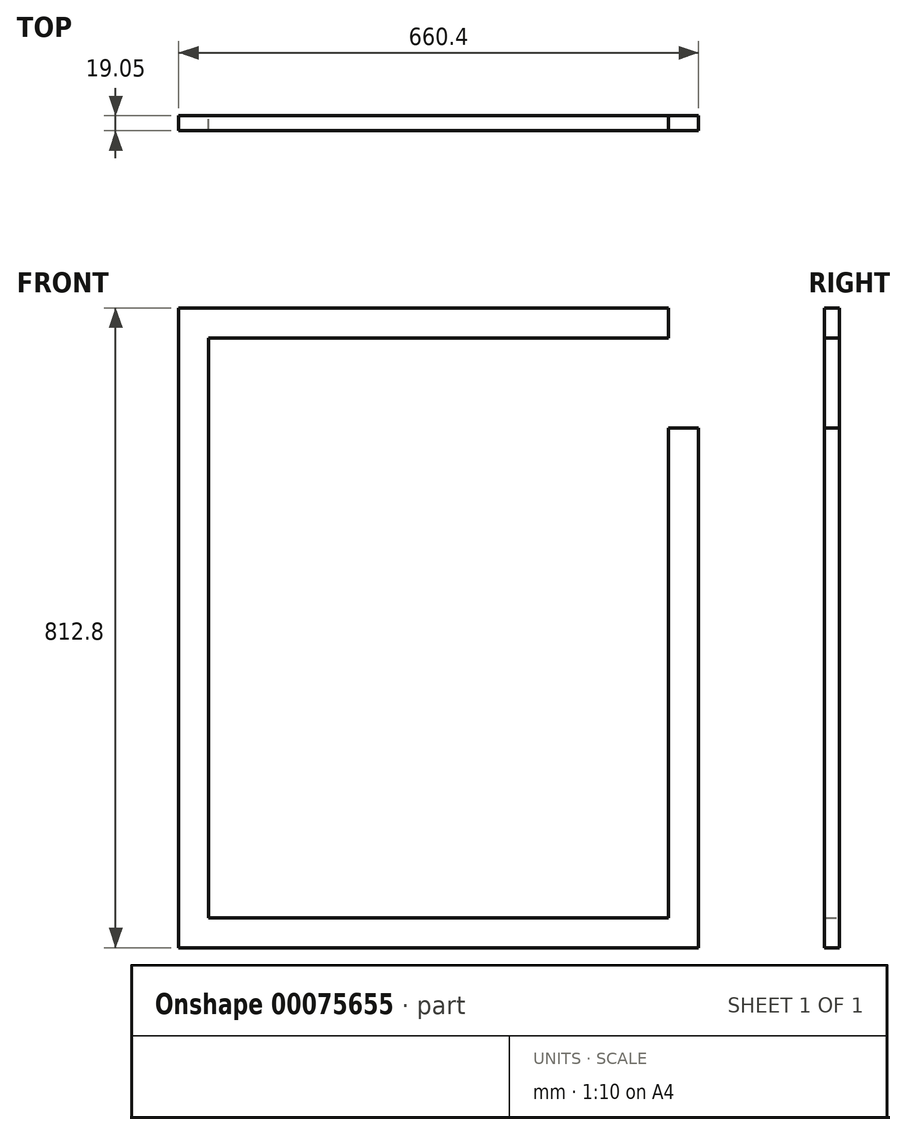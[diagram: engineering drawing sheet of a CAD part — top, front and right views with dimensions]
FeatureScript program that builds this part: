
annotation { "Feature Type Name" : "Feature", "Feature Type Description" : "" }
export const myFeature = defineFeature(function(context is Context, id is Id, definition is map)
    precondition{}
    {
        {
            var Q0;
            Q0=qCreatedBy(makeId("Front.planeOp"),FACE);
            var sketch = newSketch(context, id + "F0", { "sketchPlane" : qUnion([Q0])});
            skLineSegment(sketch, "E0.bottom", {"start": v(0, 0) * mm, "end": v(660.4, 0) * mm});
            skLineSegment(sketch, "E0.top", {"start": v(0, 812.8) * mm, "end": v(660.4, 812.8) * mm});
            skLineSegment(sketch, "E0.left", {"start": v(0, 0) * mm, "end": v(0, 812.8) * mm});
            skLineSegment(sketch, "E0.right", {"start": v(660.4, 0) * mm, "end": v(660.4, 812.8) * mm});
            skLineSegment(sketch, "E1.bottom", {"start": v(38.1, 38.1) * mm, "end": v(622.3, 38.1) * mm});
            skLineSegment(sketch, "E1.top", {"start": v(38.1, 774.7) * mm, "end": v(622.3, 774.7) * mm});
            skLineSegment(sketch, "E1.left", {"start": v(38.1, 38.1) * mm, "end": v(38.1, 774.7) * mm});
            skLineSegment(sketch, "E1.right", {"start": v(622.3, 38.1) * mm, "end": v(622.3, 774.7) * mm});
            skSolve(sketch);
        }
        {
            var Q0;
            Q0=makeQuery(id+"F0.imprint","IMPRINT",FACE,{"disambiguationData":[TD([[makeQuery(id+"F0.imprint","IMPRINT",EDGE,{"derivedFrom":sQuery(id+"F0.wireOp",EDGE,"E0.bottom")}),1.0]])]});
            extrude(context, id + "F1", {"entities" : qUnion([Q0]), "depth" : 19.05 * mm});
        }
        {
            var Q0;
            Q0=makeQuery(id+"F1.opExtrude","SWEPT_FACE",FACE,{"disambiguationData":[OSD([sQuery(id+"F0.wireOp",EDGE,"E0.top")])]});
            var sketch = newSketch(context, id + "F2", { "sketchPlane" : qUnion([Q0])});
            skLineSegment(sketch, "E2.bottom", {"start": v(660.4, -19.05) * mm, "end": v(622.3, -19.05) * mm});
            skLineSegment(sketch, "E2.top", {"start": v(660.4, 0) * mm, "end": v(622.3, 0) * mm});
            skLineSegment(sketch, "E2.left", {"start": v(660.4, -19.05) * mm, "end": v(660.4, 0) * mm});
            skLineSegment(sketch, "E2.right", {"start": v(622.3, -19.05) * mm, "end": v(622.3, 0) * mm});
            skSolve(sketch);
        }
        {
            var Q0;
            Q0=makeQuery(id+"F2.imprint","IMPRINT",FACE,{"disambiguationData":[TD([[makeQuery(id+"F2.imprint","IMPRINT",EDGE,{"derivedFrom":sQuery(id+"F2.wireOp",EDGE,"E2.bottom")}),1.0]])]});
            extrude(context, id + "F3", {"entities" : qUnion([Q0]), "operationType" : NewBodyOperationType.REMOVE, "oppositeDirection" : true, "depth" : 152.4 * mm});
        }
    });
